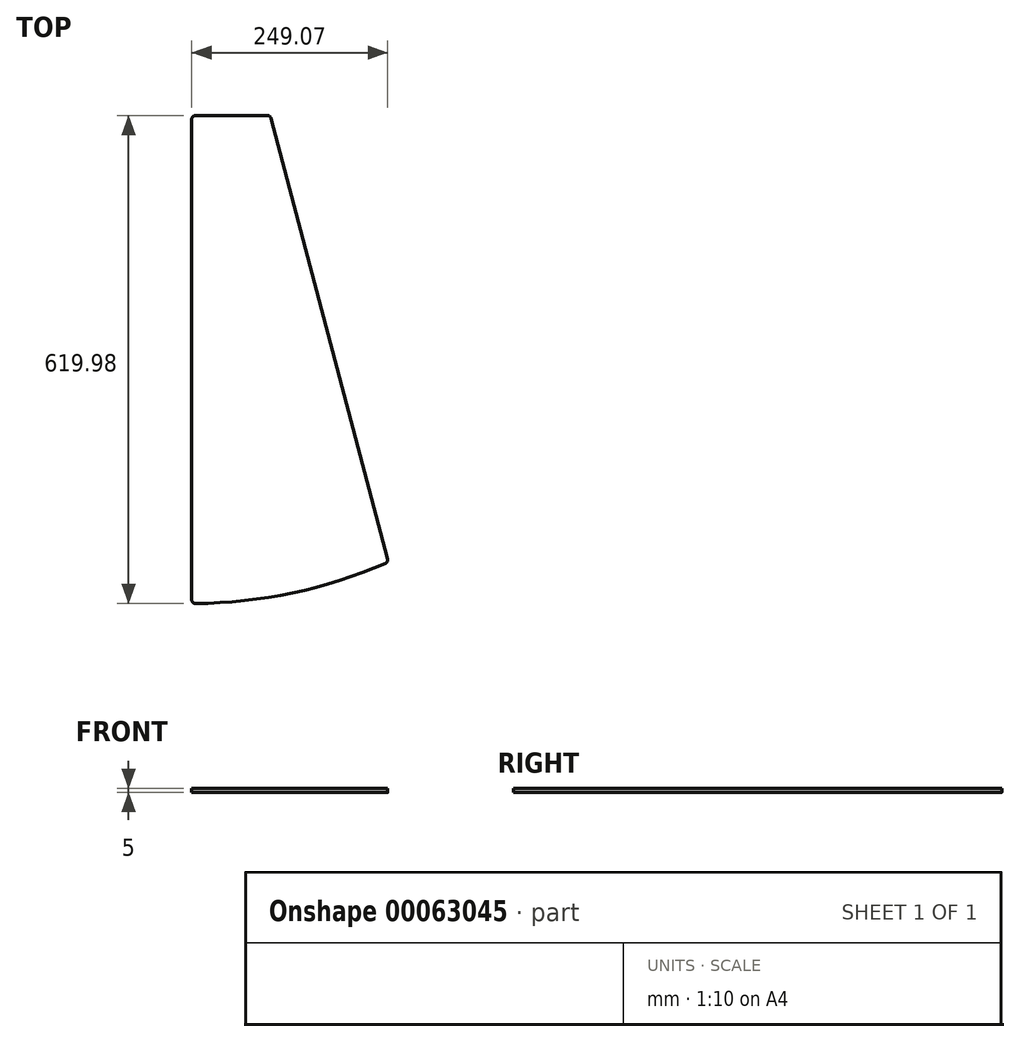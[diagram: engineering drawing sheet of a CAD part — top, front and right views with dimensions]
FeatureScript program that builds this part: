
annotation { "Feature Type Name" : "Feature", "Feature Type Description" : "" }
export const myFeature = defineFeature(function(context is Context, id is Id, definition is map)
    precondition{}
    {
        {
            var Q0;
            Q0=qCreatedBy(makeId("Top.planeOp"),FACE);
            var sketch = newSketch(context, id + "F0", { "sketchPlane" : qUnion([Q0])});
            skLineSegment(sketch, "E0", {"start": v(0, -5) * mm, "end": v(0, -614.98) * mm});
            skLineSegment(sketch, "E1", {"start": v(5, 0) * mm, "end": v(96.15, 0) * mm});
            skLineSegment(sketch, "E2", {"start": v(100.98, -3.72) * mm, "end": v(248.9, -563.22) * mm});
            skArc(sketch, "E3", {"start": v(5.04, -619.98) * mm, "mid": v(128.1, -606.62) * mm, "end": v(246.05, -569.08) * mm});
            skPoint(sketch, "E4.visualSharp", {"position": v(100, 0) * mm});
            skArc(sketch, "E4.filletArc", {"start": v(100.98, -3.72) * mm, "mid": v(99.2, -1.04) * mm, "end": v(96.15, 0) * mm});
            skArc(sketch, "E5.filletArc", {"start": v(5, 0) * mm, "mid": v(1.46, -1.46) * mm, "end": v(0, -5) * mm});
            skPoint(sketch, "E6.visualSharp", {"position": v(0, -620) * mm});
            skArc(sketch, "E6.filletArc", {"start": v(0, -614.98) * mm, "mid": v(1.48, -618.53) * mm, "end": v(5.04, -619.98) * mm});
            skPoint(sketch, "E7.visualSharp", {"position": v(250, -567.36) * mm});
            skArc(sketch, "E7.filletArc", {"start": v(246.05, -569.08) * mm, "mid": v(248.57, -566.68) * mm, "end": v(248.9, -563.22) * mm});
            skSolve(sketch);
        }
        {
            var Q0;
            Q0 = qSketchRegion(id + "F0", true);
            extrude(context, id + "F1", {"entities" : qUnion([Q0]), "depth" : 5 * mm});
        }
    });
